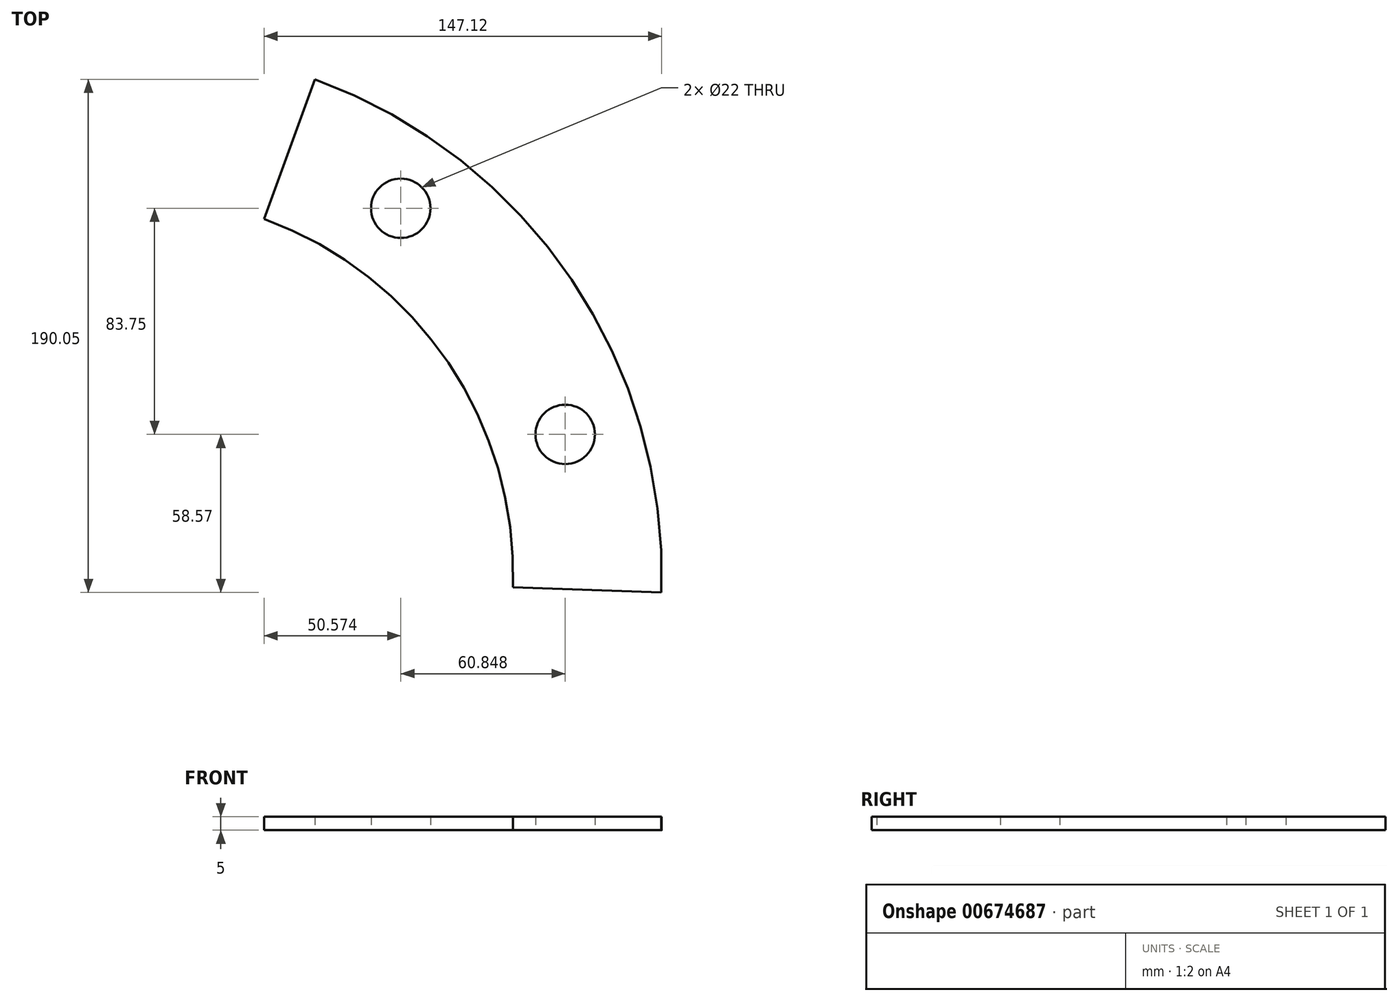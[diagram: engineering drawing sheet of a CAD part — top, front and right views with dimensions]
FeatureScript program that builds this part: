
annotation { "Feature Type Name" : "Feature", "Feature Type Description" : "" }
export const myFeature = defineFeature(function(context is Context, id is Id, definition is map)
    precondition{}
    {
        {
            var Q0;
            Q0=qCreatedBy(makeId("Top.planeOp"),FACE);
            var sketch = newSketch(context, id + "F0", { "sketchPlane" : qUnion([Q0])});
            skCircle(sketch, "E0", {"center": v(0, 0) * mm, "radius": 195 * mm});
            skLineSegment(sketch, "E1", {"start": v(-236.95, 0) * mm, "end": v(264.25, 0) * mm, "construction": true});
            skLineSegment(sketch, "E2", {"start": v(0, -228.62) * mm, "end": v(0, 236.65) * mm, "construction": true});
            skCircle(sketch, "E3", {"center": v(0, 0) * mm, "radius": 140 * mm});
            skCircle(sketch, "E4", {"center": v(0, 0) * mm, "radius": 167.5 * mm});
            skPoint(sketch, "E5", {"position": v(0, 167.5) * mm});
            skPoint(sketch, "E6.1.0", {"position": v(-98.45, 135.51) * mm});
            skPoint(sketch, "E6.2.0", {"position": v(-159.3, 51.76) * mm});
            skPoint(sketch, "E6.3.0", {"position": v(-159.3, -51.76) * mm});
            skPoint(sketch, "E6.4.0", {"position": v(-98.45, -135.51) * mm});
            skPoint(sketch, "E6.5.0", {"position": v(0, -167.5) * mm});
            skPoint(sketch, "E6.6.0", {"position": v(98.45, -135.51) * mm});
            skPoint(sketch, "E6.7.0", {"position": v(159.3, -51.76) * mm});
            skPoint(sketch, "E6.8.0", {"position": v(159.3, 51.76) * mm});
            skPoint(sketch, "E6.9.0", {"position": v(98.45, 135.51) * mm});
            skLineSegment(sketch, "E7", {"start": v(0, 0) * mm, "end": v(91.1, 250.3) * mm});
            skLineSegment(sketch, "E8", {"start": v(0, 0) * mm, "end": v(-87.39, -240.1) * mm});
            skLineSegment(sketch, "E9", {"start": v(0, 0) * mm, "end": v(-255.48, 8.92) * mm});
            skLineSegment(sketch, "E10", {"start": v(0, 0) * mm, "end": v(300.02, -10.48) * mm});
            skSolve(sketch);
        }
        {
            var Q0;
            {var subQ0=sQuery(id+"F0.wireOp",EDGE,"E7");var subQ1=sQuery(id+"F0.wireOp",EDGE,"E3");var subQ2=makeQuery(id+"F0.imprint","INTERSECT",VERTEX,{"derivedFrom":[subQ1,subQ0]});Q0=makeQuery(id+"F0.imprint","IMPRINT",FACE,{"disambiguationData":[TD([[makeQuery(id+"F0.imprint","IMPRINT",EDGE,{"disambiguationData":[TD([[subQ2,1.0]])],"derivedFrom":subQ1}),-1.0]])]});}
            var Q1;
            {var subQ0=sQuery(id+"F0.wireOp",EDGE,"E7");var subQ1=sQuery(id+"F0.wireOp",EDGE,"E0");var subQ2=makeQuery(id+"F0.imprint","INTERSECT",VERTEX,{"derivedFrom":[subQ1,subQ0]});Q1=makeQuery(id+"F0.imprint","IMPRINT",FACE,{"disambiguationData":[TD([[makeQuery(id+"F0.imprint","IMPRINT",EDGE,{"disambiguationData":[TD([[subQ2,1.0]])],"derivedFrom":subQ1}),1.0]])]});}
            extrude(context, id + "F1", {"entities" : qUnion([Q0, Q1]), "depth" : 5 * mm, "offsetDistance" : 25 * mm});
        }
        {
            var Q0;
            Q0=sQuery(id+"F0.wireOp",VERTEX,"E6.9.0");
            var Q1;
            Q1=sQuery(id+"F0.wireOp",VERTEX,"E6.8.0");
            var Q2;
            Q2=sQuery(id+"F0.wireOp",VERTEX,"E6.7.0");
            var Q3;
            Q3=makeQuery(id+"F1.opExtrude","SWEPT_BODY",BODY,{"disambiguationData":[OSD([sQuery(id+"F0.wireOp",EDGE,"E0"),sQuery(id+"F0.wireOp",EDGE,"E3"),sQuery(id+"F0.wireOp",EDGE,"E7"),sQuery(id+"F0.wireOp",EDGE,"7779584a-14d0-4c0c-a12f-be6d3e54e7f4.3.0")])]});
            hole(context, id + "F2", {"style" : HoleStyle.SIMPLE, "endStyle" : HoleEndStyle.THROUGH, "oppositeDirection" : true, "standardTappedOrClearance" : lookupTablePath({ "standard" : "ISO", "size" : "22", "type" : "Drilled" }), "standardBlindInLast" : lookupTablePath({ "standard" : "ISO", "size" : "22", "type" : "Drilled" }), "holeDiameter" : 22 * mm, "majorDiameter" : 5 * mm, "tappedDepth" : 30 * mm, "tapClearance" : 3, "locations" : qUnion([Q0, Q1, Q2]), "scope" : qUnion([Q3])});
        }
    });
